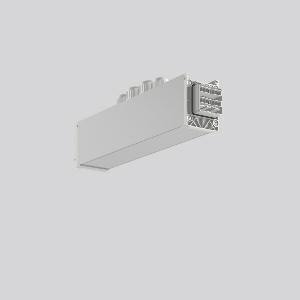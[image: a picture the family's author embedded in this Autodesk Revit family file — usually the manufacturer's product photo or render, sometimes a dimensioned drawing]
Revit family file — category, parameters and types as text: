
# Revit family: linedo_mitteleinspeisung_7pol_s_s_982698_000_5_89da
name_source: partatom
category: Lighting Fixtures
units: mm (PartAtom-declared; Revit-internal decimal feet)

## family parameters
Cut with Voids When Loaded = No
Host = Face
Light Source = No
Part Type = Normal
Room Calculation Point = No
Round Connector Dimension = Use Diameter
Shared = No

## types (1)
- LINEDO_Mitteleinspeisung_7pol_S_S
    Apparent Load = 0 VA
    Default Elevation = 1800 mm
    Description = Series: LINEDO
Middle power feed, 7-pole, connection plug / plug. Housing: extruded aluminium profile, anodised. Cover made of plastic, surface like housing. LINEDO plug system, plastic, light grey. 4 cable glands (2 x M20 and 2 x M25). Cable glands on top. Easy connection for rigid or flexible wires.
Colour: anodised aluminium
Length: 349 mm
Width: 58 mm
Height: 76 mm
Weight: 751 g
    Height = 76 mm
    Lamp = 0 x
    Length = 349 mm
    Luminous efficacy = 0 lm/W
    Manufacturer = RZB
    ModVariant = No
    Model = 982698.000.5
    Mounting Place = Ceiling
    Mounting Type = Surface mounted, Pendant
    Number of Poles = 1
    OnlyDefault = Yes
    Power Factor = 1
    Product Name = LINEDO_Mitteleinspeisung_7pol_S_S
    Product group = Continuous line luminaire system Linedo IP 54
    ProductGroupID = 314
    Protection Class = Protection class I
    Protection Degree = IP 54
    RLX_Detail_Level = 1
    RLX_Emergency_Light_Flux = 0 lm
    RLX_Emergency_Type = 0
    RLX_Emergency_Type_DB = No
    RlxData = <blob elided: 21945 chars, md5=d0cf66a8>
    Standby Power = 0 W
    System Light Flux = 0 lm
    System Power = 0 W
    Type Comments = Product without accessories
    Type Image = 982698.000.2.jpg
    URL = http://relux.com
    VarID = ---
    Voltage = 0 V
    Weight = 0.00 kg
    Width = 58 mm

## geometry (parser evidence)
native form markers: Blend x4, Sweep x10
no freeform markers — native parametric forms only
